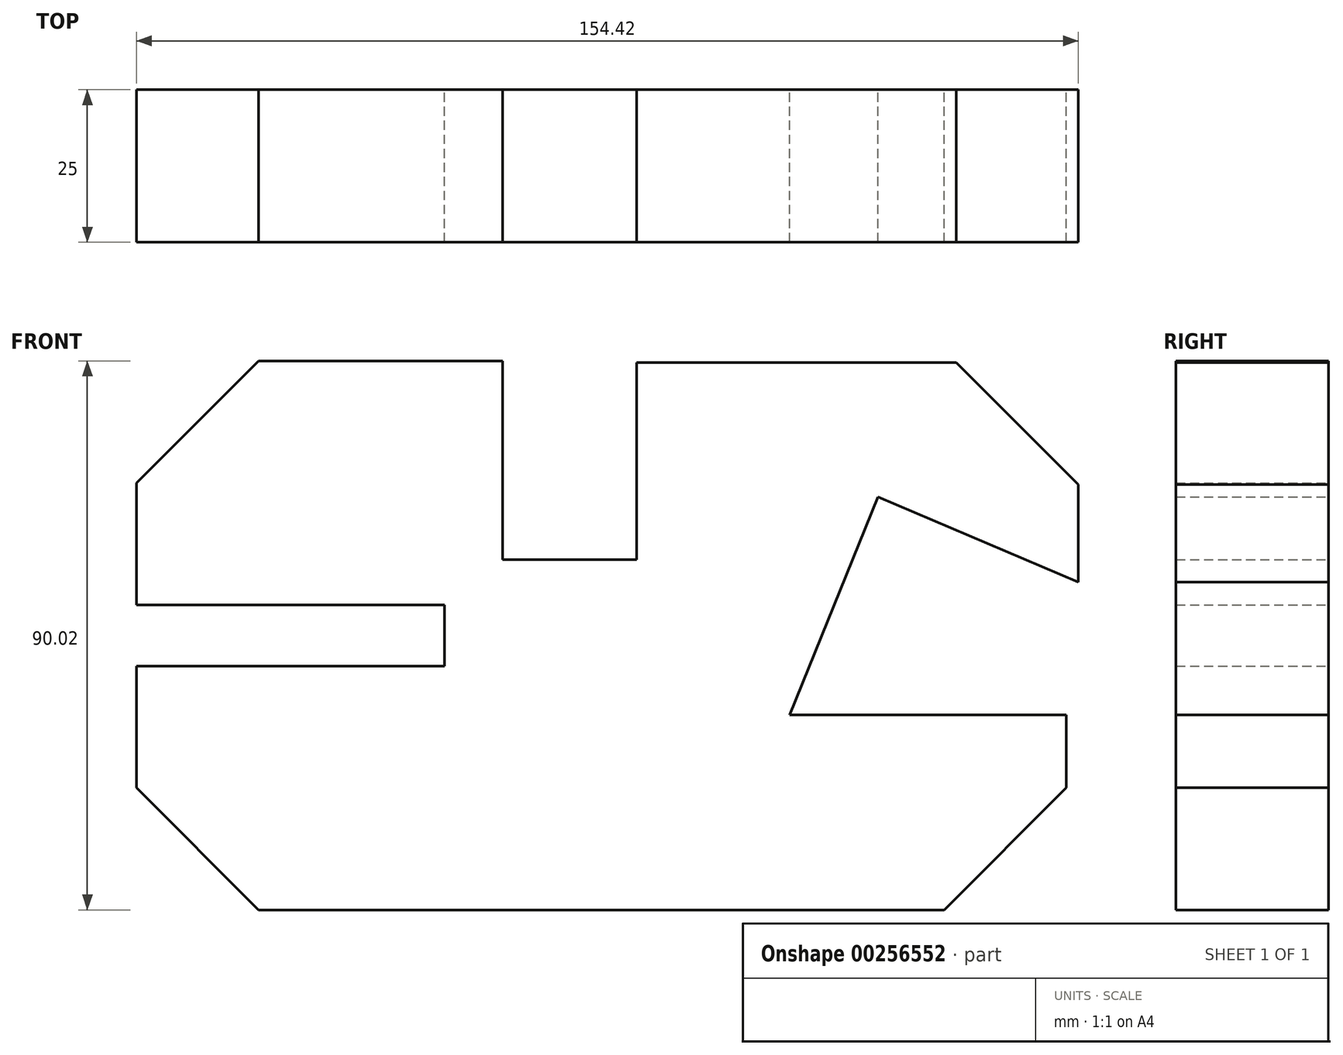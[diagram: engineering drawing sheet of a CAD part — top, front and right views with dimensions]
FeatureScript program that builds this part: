
annotation { "Feature Type Name" : "Feature", "Feature Type Description" : "" }
export const myFeature = defineFeature(function(context is Context, id is Id, definition is map)
    precondition{}
    {
        {
            var Q0;
            Q0=qCreatedBy(makeId("Front.planeOp"),FACE);
            var sketch = newSketch(context, id + "F0", { "sketchPlane" : qUnion([Q0])});
            skLineSegment(sketch, "E0", {"start": v(-30.33, 59.03) * mm, "end": v(9.67, 59.03) * mm});
            skLineSegment(sketch, "E1", {"start": v(31.67, 58.77) * mm, "end": v(31.67, 26.47) * mm});
            skLineSegment(sketch, "E2", {"start": v(9.67, 26.47) * mm, "end": v(31.67, 26.47) * mm});
            skLineSegment(sketch, "E3", {"start": v(9.67, 26.47) * mm, "end": v(9.67, 59.03) * mm});
            skLineSegment(sketch, "E4", {"start": v(31.67, 58.77) * mm, "end": v(84.07, 58.77) * mm});
            skLineSegment(sketch, "E5", {"start": v(84.07, 58.77) * mm, "end": v(104.08, 38.76) * mm});
            skLineSegment(sketch, "E6", {"start": v(104.08, 38.76) * mm, "end": v(104.08, 22.76) * mm});
            skLineSegment(sketch, "E7", {"start": v(-30.33, 59.03) * mm, "end": v(-50.34, 39.02) * mm});
            skLineSegment(sketch, "E8", {"start": v(-50.34, 39.02) * mm, "end": v(-50.34, 19.02) * mm});
            skLineSegment(sketch, "E9", {"start": v(-50.34, 19.02) * mm, "end": v(0.16, 19.02) * mm});
            skLineSegment(sketch, "E10", {"start": v(0.16, 19.02) * mm, "end": v(0.16, 9.02) * mm});
            skLineSegment(sketch, "E11", {"start": v(-50.34, 9.02) * mm, "end": v(0.16, 9.02) * mm});
            skLineSegment(sketch, "E12", {"start": v(-50.34, 9.02) * mm, "end": v(-50.34, -10.98) * mm});
            skLineSegment(sketch, "E13", {"start": v(-50.34, -10.98) * mm, "end": v(-30.33, -31) * mm});
            skLineSegment(sketch, "E14", {"start": v(-30.33, -31) * mm, "end": v(82.07, -31) * mm});
            skLineSegment(sketch, "E15", {"start": v(82.07, -31) * mm, "end": v(102.08, -10.98) * mm});
            skLineSegment(sketch, "E16", {"start": v(102.08, -10.98) * mm, "end": v(102.08, 1.02) * mm});
            skLineSegment(sketch, "E17", {"start": v(102.08, 1.02) * mm, "end": v(56.78, 1.02) * mm});
            skLineSegment(sketch, "E18", {"start": v(56.78, 1.02) * mm, "end": v(71.2, 36.72) * mm});
            skLineSegment(sketch, "E19", {"start": v(71.2, 36.72) * mm, "end": v(104.08, 22.76) * mm});
            skSolve(sketch);
        }
        {
            var Q0;
            Q0=makeQuery(id+"F0.imprint","IMPRINT",FACE,{"disambiguationData":[TD([[makeQuery(id+"F0.imprint","IMPRINT",EDGE,{"derivedFrom":sQuery(id+"F0.wireOp",EDGE,"E0")}),-1.0]])]});
            extrude(context, id + "F1", {"entities" : qUnion([Q0]), "depth" : 25 * mm});
        }
    });
